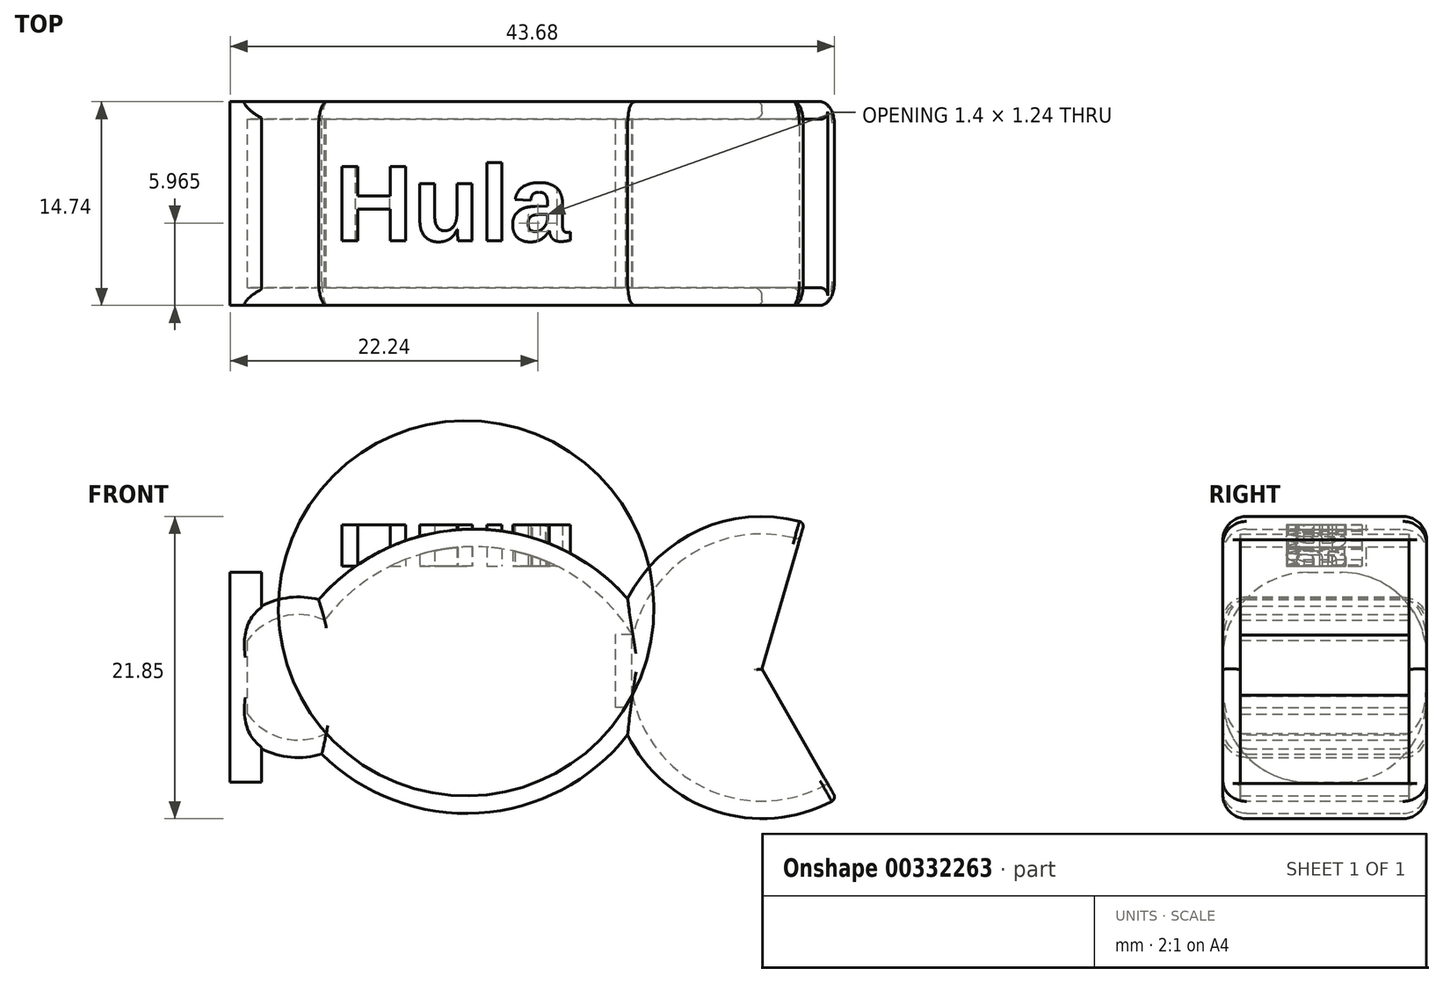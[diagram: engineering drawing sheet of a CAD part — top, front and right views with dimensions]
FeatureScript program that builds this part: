
annotation { "Feature Type Name" : "Feature", "Feature Type Description" : "" }
export const myFeature = defineFeature(function(context is Context, id is Id, definition is map)
    precondition{}
    {
        {
            var Q0;
            Q0=qCreatedBy(makeId("Front.planeOp"),FACE);
            var sketch = newSketch(context, id + "F0", { "sketchPlane" : qUnion([Q0])});
            skArc(sketch, "E0", {"start": v(13.64, 12.88) * mm, "mid": v(3.1, 10.38) * mm, "end": v(0, 0) * mm});
            skArc(sketch, "E1", {"start": v(0, 0) * mm, "mid": v(6.18, -7.58) * mm, "end": v(15.94, -7.09) * mm});
            skLineSegment(sketch, "E2", {"start": v(13.64, 12.88) * mm, "end": v(10.57, 2.3) * mm});
            skLineSegment(sketch, "E3", {"start": v(15.94, -7.09) * mm, "end": v(10.57, 2.3) * mm});
            skArc(sketch, "E4", {"start": v(-21.99, -3.06) * mm, "mid": v(-10.42, -8.13) * mm, "end": v(0.86, -2.46) * mm});
            skArc(sketch, "E5", {"start": v(0.86, 7.38) * mm, "mid": v(-10.73, 12.41) * mm, "end": v(-21.99, 6.7) * mm});
            skCircle(sketch, "E6", {"center": v(-22.94, 1.7) * mm, "radius": 5.8 * mm});
            skLineSegment(sketch, "E7.bottom", {"start": v(-27.87, -5.88) * mm, "end": v(-25.6, -5.88) * mm});
            skLineSegment(sketch, "E7.top", {"start": v(-27.87, 9.29) * mm, "end": v(-25.6, 9.29) * mm});
            skLineSegment(sketch, "E7.left", {"start": v(-27.87, -5.88) * mm, "end": v(-27.87, 9.29) * mm});
            skLineSegment(sketch, "E7.right", {"start": v(-25.6, -5.88) * mm, "end": v(-25.6, 9.29) * mm});
            skPoint(sketch, "E7.middle", {"position": v(-26.73, 1.7) * mm});
            skSolve(sketch);
        }
        {
            var Q0;
            {var subQ6=sQuery(id+"F0.wireOp",EDGE,"E2");Q0=makeQuery(id+"F0.imprint","IMPRINT",FACE,{"disambiguationData":[TD([[makeQuery(id+"F0.imprint","IMPRINT",EDGE,{"derivedFrom":subQ6}),-1.0]])]});}
            var Q1;
            {var subQ1=sQuery(id+"F0.wireOp",EDGE,"E0");var subQ5=sQuery(id+"F0.wireOp",EDGE,"E1");var subQ6=makeQuery(id+"F0.imprint","INTERSECT",VERTEX,{"derivedFrom":[subQ1,subQ5]});Q1=makeQuery(id+"F0.imprint","IMPRINT",FACE,{"disambiguationData":[TD([[makeQuery(id+"F0.imprint","IMPRINT",EDGE,{"disambiguationData":[TD([[subQ6,1.0]])],"derivedFrom":subQ1}),-1.0]])]});}
            var Q2;
            {var subQ0=sQuery(id+"F0.wireOp",EDGE,"E6");var subQ1=makeQuery(id+"F0.imprint","INTERSECT",VERTEX,{"derivedFrom":[sQuery(id+"F0.wireOp",EDGE,"E5"),subQ0]});Q2=makeQuery(id+"F0.imprint","IMPRINT",FACE,{"disambiguationData":[TD([[makeQuery(id+"F0.imprint","IMPRINT",EDGE,{"disambiguationData":[TD([[subQ1,-1.0]])],"derivedFrom":subQ0}),1.0]])]});}
            var Q3;
            {var subQ5=sQuery(id+"F0.wireOp",EDGE,"E7.top");Q3=makeQuery(id+"F0.imprint","IMPRINT",FACE,{"disambiguationData":[TD([[makeQuery(id+"F0.imprint","IMPRINT",EDGE,{"derivedFrom":subQ5}),-1.0]])]});}
            var Q4;
            {var subQ0=sQuery(id+"F0.wireOp",EDGE,"E7.right");var subQ1=sQuery(id+"F0.wireOp",EDGE,"E6");var subQ2=makeQuery(id+"F0.imprint","INTERSECT",VERTEX,{"disambiguationData":[OD(0.0)],"derivedFrom":[subQ1,subQ0]});Q4=makeQuery(id+"F0.imprint","IMPRINT",FACE,{"disambiguationData":[TD([[makeQuery(id+"F0.imprint","IMPRINT",EDGE,{"disambiguationData":[TD([[subQ2,-1.0]])],"derivedFrom":subQ1}),1.0]])]});}
            var Q5;
            {var subQ5=sQuery(id+"F0.wireOp",EDGE,"E7.bottom");Q5=makeQuery(id+"F0.imprint","IMPRINT",FACE,{"disambiguationData":[TD([[makeQuery(id+"F0.imprint","IMPRINT",EDGE,{"derivedFrom":subQ5}),1.0]])]});}
            var Q6;
            {var subQ0=sQuery(id+"F0.wireOp",EDGE,"E7.left");var subQ1=sQuery(id+"F0.wireOp",EDGE,"E6");var subQ2=makeQuery(id+"F0.imprint","INTERSECT",VERTEX,{"disambiguationData":[OD(0.0)],"derivedFrom":[subQ1,subQ0]});Q6=makeQuery(id+"F0.imprint","IMPRINT",FACE,{"disambiguationData":[TD([[makeQuery(id+"F0.imprint","IMPRINT",EDGE,{"disambiguationData":[TD([[subQ2,-1.0]])],"derivedFrom":subQ1}),1.0]])]});}
            extrude(context, id + "F1", {"entities" : qUnion([Q0, Q1, Q2, Q3, Q4, Q5, Q6]), "endBound" : BoundingType.SYMMETRIC, "depth" : 14.73 * mm});
        }
        {
            var Q0;
            Q0=makeQuery(id+"F1.opExtrude","SWEPT_FACE",FACE,{"disambiguationData":[OSD([sQuery(id+"F0.wireOp",EDGE,"E3")])]});
            var Q1;
            Q1=makeQuery(id+"F1.opExtrude","SWEPT_FACE",FACE,{"disambiguationData":[OSD([sQuery(id+"F0.wireOp",EDGE,"E2")])]});
            shell(context, id + "F2", {"entities" : qUnion([Q0, Q1]), "thickness" : 1.27 * mm});
        }
        {
            var Q0;
            Q0=qCreatedBy(makeId("Right.planeOp"),FACE);
            var sketch = newSketch(context, id + "F3", { "sketchPlane" : qUnion([Q0])});
            skLineSegment(sketch, "E8.bottom", {"start": v(-6.09, -0.47) * mm, "end": v(6.09, -0.47) * mm});
            skLineSegment(sketch, "E8.top", {"start": v(-6.09, 4.8) * mm, "end": v(6.09, 4.8) * mm});
            skLineSegment(sketch, "E8.left", {"start": v(-6.09, -0.47) * mm, "end": v(-6.09, 4.8) * mm});
            skLineSegment(sketch, "E8.right", {"start": v(6.09, -0.47) * mm, "end": v(6.09, 4.8) * mm});
            skPoint(sketch, "E8.middle", {"position": v(0, 2.17) * mm});
            skSolve(sketch);
        }
        {
            var Q0;
            Q0=makeQuery(id+"F3.imprint","IMPRINT",FACE,{"disambiguationData":[TD([[makeQuery(id+"F3.imprint","IMPRINT",EDGE,{"derivedFrom":sQuery(id+"F3.wireOp",EDGE,"E8.bottom")}),1.0]])]});
            extrude(context, id + "F4", {"entities" : qUnion([Q0]), "operationType" : NewBodyOperationType.ADD, "depth" : 1.17 * mm});
        }
        {
            var Q0;
            Q0=makeQuery(id+"F1.opExtrude","CAP_EDGE",EDGE,{"disambiguationData":[OSD([sQuery(id+"F0.wireOp",EDGE,"E5")])],"isStart":false});
            var Q1;
            Q1=makeQuery(id+"F1.opExtrude","CAP_EDGE",EDGE,{"disambiguationData":[OSD([sQuery(id+"F0.wireOp",EDGE,"E4")])],"isStart":false});
            var Q2;
            Q2=makeQuery(id+"F1.opExtrude","CAP_EDGE",EDGE,{"disambiguationData":[OSD([sQuery(id+"F0.wireOp",EDGE,"E0")])],"isStart":false});
            var Q3;
            Q3=makeQuery(id+"F1.opExtrude","CAP_EDGE",EDGE,{"disambiguationData":[OSD([sQuery(id+"F0.wireOp",EDGE,"E1")])],"isStart":false});
            var Q4;
            {var subQ0=sQuery(id+"F0.wireOp",EDGE,"E6");Q4=makeQuery(id+"F1.opExtrude","CAP_EDGE",EDGE,{"disambiguationData":[OSD([subQ0]),TDD([makeQuery(id+"F0.imprint","IMPRINT",EDGE,{"disambiguationData":[TD([[makeQuery(id+"F0.imprint","INTERSECT",VERTEX,{"derivedFrom":[sQuery(id+"F0.wireOp",EDGE,"E5"),subQ0]}),-1.0]])],"derivedFrom":subQ0})])],"isStart":false});}
            var Q5;
            {var subQ0=sQuery(id+"F0.wireOp",EDGE,"E6");Q5=makeQuery(id+"F1.opExtrude","CAP_EDGE",EDGE,{"disambiguationData":[OSD([subQ0]),TDD([makeQuery(id+"F0.imprint","IMPRINT",EDGE,{"disambiguationData":[TD([[makeQuery(id+"F0.imprint","INTERSECT",VERTEX,{"derivedFrom":[sQuery(id+"F0.wireOp",EDGE,"E4"),subQ0]}),1.0]])],"derivedFrom":subQ0})])],"isStart":false});}
            var Q6;
            Q6=makeQuery(id+"F1.opExtrude","CAP_EDGE",EDGE,{"disambiguationData":[OSD([sQuery(id+"F0.wireOp",EDGE,"E0")])],"isStart":true});
            var Q7;
            Q7=makeQuery(id+"F1.opExtrude","CAP_EDGE",EDGE,{"disambiguationData":[OSD([sQuery(id+"F0.wireOp",EDGE,"E1")])],"isStart":true});
            var Q8;
            Q8=makeQuery(id+"F1.opExtrude","CAP_EDGE",EDGE,{"disambiguationData":[OSD([sQuery(id+"F0.wireOp",EDGE,"E4")])],"isStart":true});
            var Q9;
            Q9=makeQuery(id+"F1.opExtrude","CAP_EDGE",EDGE,{"disambiguationData":[OSD([sQuery(id+"F0.wireOp",EDGE,"E5")])],"isStart":true});
            var Q10;
            {var subQ0=sQuery(id+"F0.wireOp",EDGE,"E6");Q10=makeQuery(id+"F1.opExtrude","CAP_EDGE",EDGE,{"disambiguationData":[OSD([subQ0]),TDD([makeQuery(id+"F0.imprint","IMPRINT",EDGE,{"disambiguationData":[TD([[makeQuery(id+"F0.imprint","INTERSECT",VERTEX,{"derivedFrom":[sQuery(id+"F0.wireOp",EDGE,"E5"),subQ0]}),-1.0]])],"derivedFrom":subQ0})])],"isStart":true});}
            var Q11;
            {var subQ0=sQuery(id+"F0.wireOp",EDGE,"E6");Q11=makeQuery(id+"F1.opExtrude","CAP_EDGE",EDGE,{"disambiguationData":[OSD([subQ0]),TDD([makeQuery(id+"F0.imprint","IMPRINT",EDGE,{"disambiguationData":[TD([[makeQuery(id+"F0.imprint","INTERSECT",VERTEX,{"derivedFrom":[sQuery(id+"F0.wireOp",EDGE,"E4"),subQ0]}),1.0]])],"derivedFrom":subQ0})])],"isStart":true});}
            fillet(context, id + "F5", {"entities" : qUnion([Q0, Q1, Q2, Q3, Q4, Q5, Q6, Q7, Q8, Q9, Q10, Q11]), "radius" : 1.72 * mm, "tangentPropagation" : true, "allowEdgeOverflow" : false});
        }
        {
            var Q0;
            Q0=makeQuery(id+"F1.opExtrude","CAP_EDGE",EDGE,{"disambiguationData":[OSD([sQuery(id+"F0.wireOp",EDGE,"E2")])],"isStart":true});
            var Q1;
            Q1=makeQuery(id+"F1.opExtrude","CAP_EDGE",EDGE,{"disambiguationData":[OSD([sQuery(id+"F0.wireOp",EDGE,"E3")])],"isStart":true});
            var Q2;
            Q2=makeQuery(id+"F1.opExtrude","CAP_EDGE",EDGE,{"disambiguationData":[OSD([sQuery(id+"F0.wireOp",EDGE,"E3")])],"isStart":false});
            var Q3;
            Q3=makeQuery(id+"F1.opExtrude","CAP_EDGE",EDGE,{"disambiguationData":[OSD([sQuery(id+"F0.wireOp",EDGE,"E2")])],"isStart":false});
            fillet(context, id + "F6", {"entities" : qUnion([Q0, Q1, Q2, Q3]), "radius" : 0.37 * mm, "tangentPropagation" : true, "allowEdgeOverflow" : false});
        }
        {
            var Q0;
            {var subQ0=sQuery(id+"F0.wireOp",EDGE,"E3");Q0=makeQuery(id+"F2.opShell","OFFSET_EDGE",EDGE,{"disambiguationData":[OSD([subQ0]),TDD([makeQuery(id+"F1.opExtrude","CAP_EDGE",EDGE,{"disambiguationData":[OSD([subQ0])],"isStart":true})])]});}
            var Q1;
            {var subQ0=sQuery(id+"F0.wireOp",EDGE,"E2");Q1=makeQuery(id+"F2.opShell","OFFSET_EDGE",EDGE,{"disambiguationData":[OSD([subQ0]),TDD([makeQuery(id+"F1.opExtrude","CAP_EDGE",EDGE,{"disambiguationData":[OSD([subQ0])],"isStart":false})])]});}
            var Q2;
            {var subQ0=sQuery(id+"F0.wireOp",EDGE,"E2");Q2=makeQuery(id+"F2.opShell","OFFSET_EDGE",EDGE,{"disambiguationData":[OSD([subQ0]),TDD([makeQuery(id+"F1.opExtrude","CAP_EDGE",EDGE,{"disambiguationData":[OSD([subQ0])],"isStart":true})])]});}
            var Q3;
            {var subQ0=sQuery(id+"F0.wireOp",EDGE,"E3");Q3=makeQuery(id+"F2.opShell","OFFSET_EDGE",EDGE,{"disambiguationData":[OSD([subQ0]),TDD([makeQuery(id+"F1.opExtrude","CAP_EDGE",EDGE,{"disambiguationData":[OSD([subQ0])],"isStart":false})])]});}
            fillet(context, id + "F7", {"entities" : qUnion([Q0, Q1, Q2, Q3]), "radius" : 0.55 * mm, "tangentPropagation" : true, "allowEdgeOverflow" : false});
        }
        {
            var Q0;
            Q0=makeQuery(id+"F1.opExtrude","CAP_EDGE",EDGE,{"disambiguationData":[OSD([sQuery(id+"F0.wireOp",EDGE,"E7.bottom")])],"isStart":true});
            var Q1;
            Q1=makeQuery(id+"F1.opExtrude","CAP_EDGE",EDGE,{"disambiguationData":[OSD([sQuery(id+"F0.wireOp",EDGE,"E7.top")])],"isStart":true});
            var Q2;
            Q2=makeQuery(id+"F1.opExtrude","CAP_EDGE",EDGE,{"disambiguationData":[OSD([sQuery(id+"F0.wireOp",EDGE,"E7.top")])],"isStart":false});
            var Q3;
            Q3=makeQuery(id+"F1.opExtrude","CAP_EDGE",EDGE,{"disambiguationData":[OSD([sQuery(id+"F0.wireOp",EDGE,"E7.bottom")])],"isStart":false});
            fillet(context, id + "F8", {"entities" : qUnion([Q0, Q1, Q2, Q3]), "radius" : 6.13 * mm, "tangentPropagation" : true, "allowEdgeOverflow" : false});
        }
        {
            var Q0;
            Q0=qCreatedBy(makeId("Top.planeOp"),FACE);
            var sketch = newSketch(context, id + "F9", { "sketchPlane" : qUnion([Q0])});
            skText(sketch, "E9", { "text": "Hula", "fontName": "Arimo-Bold.ttf"});
            const initialGuessF9  = {"E9": [-0.0203, -0.0027, 1, 0, 0.00564]};
            skSetInitialGuess(sketch, initialGuessF9);
            skSolve(sketch);
        }
        {
            var Q0;
            Q0 = qSketchRegion(id + "F9", true);
            var Q1;
            Q1 = qConstructionFilter(qBodyType(qCreatedBy(id + "F9" ,EDGE), BodyType.WIRE), ConstructionObject.NO);
            extrude(context, id + "F10", {"entities" : qUnion([Q0]), "operationType" : NewBodyOperationType.ADD, "surfaceEntities" : qUnion([Q1]), "depth" : 12.73 * mm, "hasSecondDirection" : true, "secondDirectionOppositeDirection" : false, "secondDirectionDepth" : 9.73 * mm});
        }
    });
